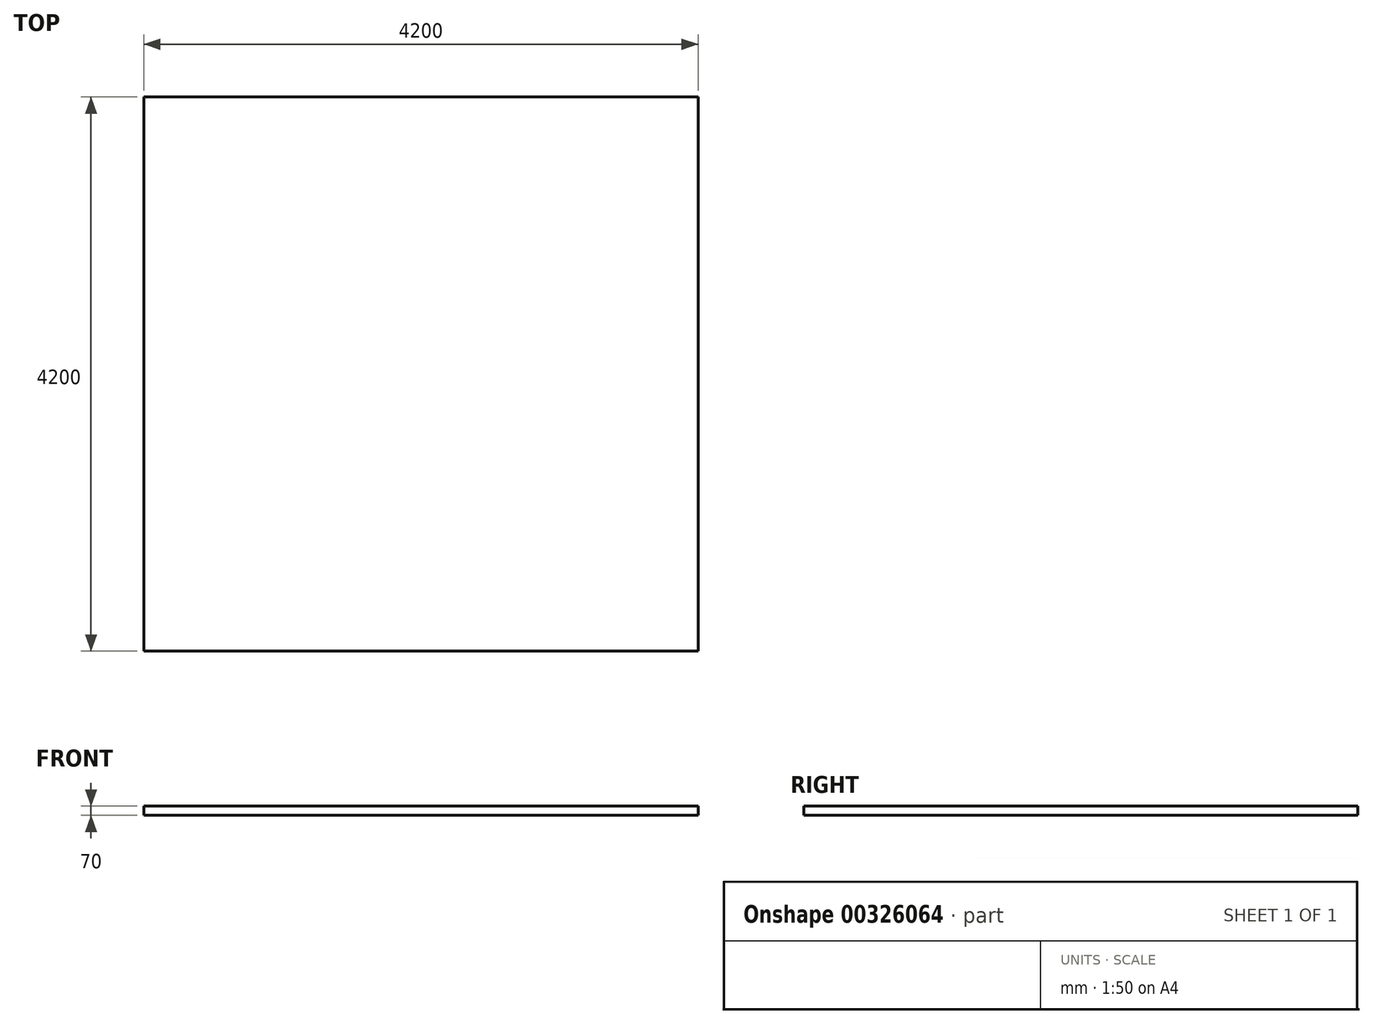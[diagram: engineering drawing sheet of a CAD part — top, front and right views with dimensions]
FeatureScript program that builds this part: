
annotation { "Feature Type Name" : "Feature", "Feature Type Description" : "" }
export const myFeature = defineFeature(function(context is Context, id is Id, definition is map)
    precondition{}
    {
        {
            var Q0;
            Q0=qCreatedBy(makeId("Top.planeOp"),FACE);
            var sketch = newSketch(context, id + "F0", { "sketchPlane" : qUnion([Q0])});
            skLineSegment(sketch, "E0.bottom", {"start": v(2100, -2100) * mm, "end": v(-2100, -2100) * mm});
            skLineSegment(sketch, "E0.top", {"start": v(2100, 2100) * mm, "end": v(-2100, 2100) * mm});
            skLineSegment(sketch, "E0.left", {"start": v(2100, -2100) * mm, "end": v(2100, 2100) * mm});
            skLineSegment(sketch, "E0.right", {"start": v(-2100, -2100) * mm, "end": v(-2100, 2100) * mm});
            skPoint(sketch, "E0.middle", {"position": v(0, 0) * mm});
            skSolve(sketch);
        }
        {
            var Q0;
            Q0=makeQuery(id+"F0.imprint","IMPRINT",FACE,{"disambiguationData":[TD([[makeQuery(id+"F0.imprint","IMPRINT",EDGE,{"derivedFrom":sQuery(id+"F0.wireOp",EDGE,"E0.bottom")}),-1.0]])]});
            extrude(context, id + "F1", {"entities" : qUnion([Q0]), "oppositeDirection" : true, "depth" : 70 * mm});
        }
    });
